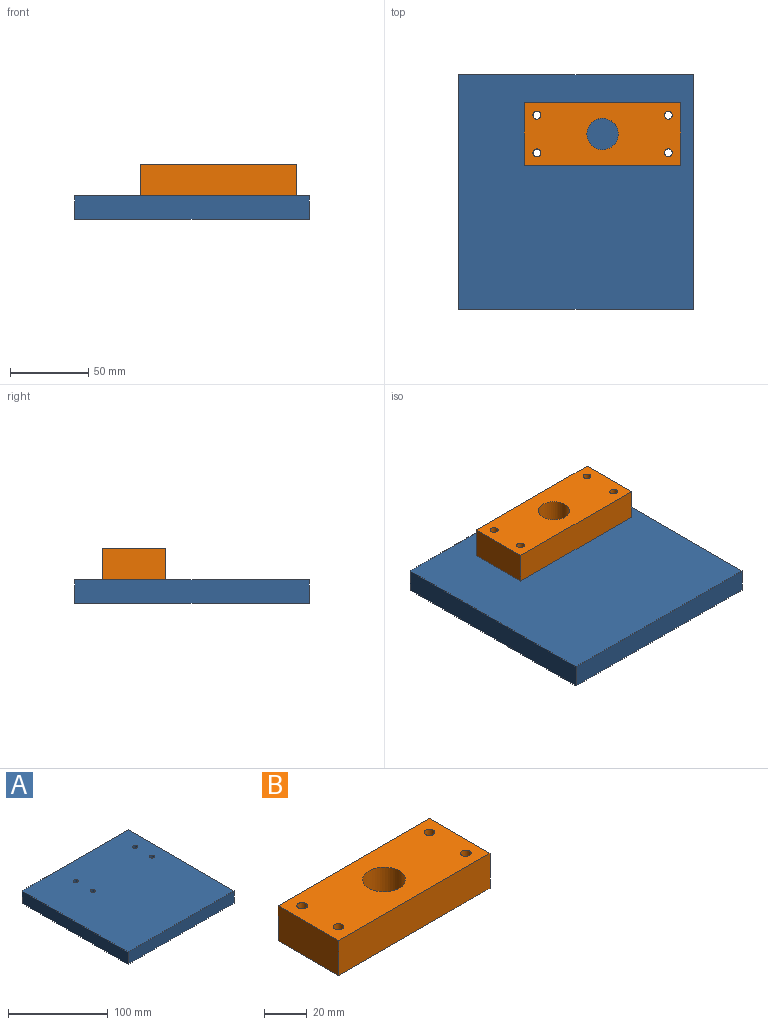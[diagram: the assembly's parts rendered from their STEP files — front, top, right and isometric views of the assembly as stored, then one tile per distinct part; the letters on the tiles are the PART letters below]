
ASSEMBLY  parts=2 mates=3
PART A: 10 faces, bbox 150x150x15 mm
  f0: plane 150x15mm, normal (-1,0,0), area 2250mm2, adj f1,f6,f8,f9
  f1: plane 150x15mm, normal (0,-1,0), area 2250mm2, adj f0,f2,f8,f9
  f2: plane 150x15mm, normal (1,0,0), area 2250mm2, adj f1,f6,f8,f9
  f3: cylinder r=2.5mm len=15mm, axis (0,0,-1), area 235.6mm2, adj f8,f9
  f4: cylinder r=2.5mm len=15mm, axis (0,0,-1), area 235.6mm2, adj f8,f9
  f5: cylinder r=2.5mm len=15mm, axis (0,0,-1), area 235.6mm2, adj f8,f9
  f6: plane 150x15mm, normal (0,1,0), area 2250mm2, adj f0,f2,f8,f9
  f7: cylinder r=2.5mm len=15mm, axis (0,0,-1), area 235.6mm2, adj f8,f9
  f8: plane 150x150mm, normal (0,0,1), area 22421.5mm2, adj f0,f1,f2,f3,f4,f5,f6,f7
  f9: plane 150x150mm, normal (0,0,-1), area 22421.5mm2, adj f0,f1,f2,f3,f4,f5,f6,f7
PART B: 11 faces, bbox 100x40x20 mm
  f0: plane 40x20mm, normal (-1,0,0), area 800mm2, adj f1,f7,f9,f10
  f1: plane 100x20mm, normal (0,-1,0), area 2000mm2, adj f0,f2,f9,f10
  f2: plane 40x20mm, normal (1,0,0), area 800mm2, adj f1,f7,f9,f10
  f3: cylinder r=2.5mm len=20mm, axis (0,0,-1), area 314.2mm2, adj f9,f10
  f4: cylinder r=2.5mm len=20mm, axis (0,0,-1), area 314.2mm2, adj f9,f10
  f5: cylinder r=2.5mm len=20mm, axis (0,0,-1), area 314.2mm2, adj f9,f10
  f6: cylinder r=10mm len=20mm, axis (0,0,-1), area 1256.6mm2, adj f9,f10
  f7: plane 100x20mm, normal (0,1,0), area 2000mm2, adj f0,f2,f9,f10
  f8: cylinder r=2.5mm len=20mm, axis (0,0,-1), area 314.2mm2, adj f9,f10
  f9: plane 100x40mm, normal (0,0,1), area 3607.3mm2, adj f0,f1,f2,f3,f4,f5,f6,f7
  f10: plane 100x40mm, normal (0,0,-1), area 3607.3mm2, adj f0,f1,f2,f3,f4,f5,f6,f7
PLACE A t=(20.8,-170.52,108.57)mm
PLACE B t=(62.8,-78.52,123.57)mm
MATE cylindrical A.f4 <-> B.f5  axis (0,0,1) through (70.8,-70.52,123.57)mm
MATE planar B.f6 <-> A.f8  axis (0,0,-1) through (112.8,-58.52,123.57)mm
MATE cylindrical A.f5 <-> A.f9  axis (0,0,1) through (70.8,-46.52,123.57)mm
